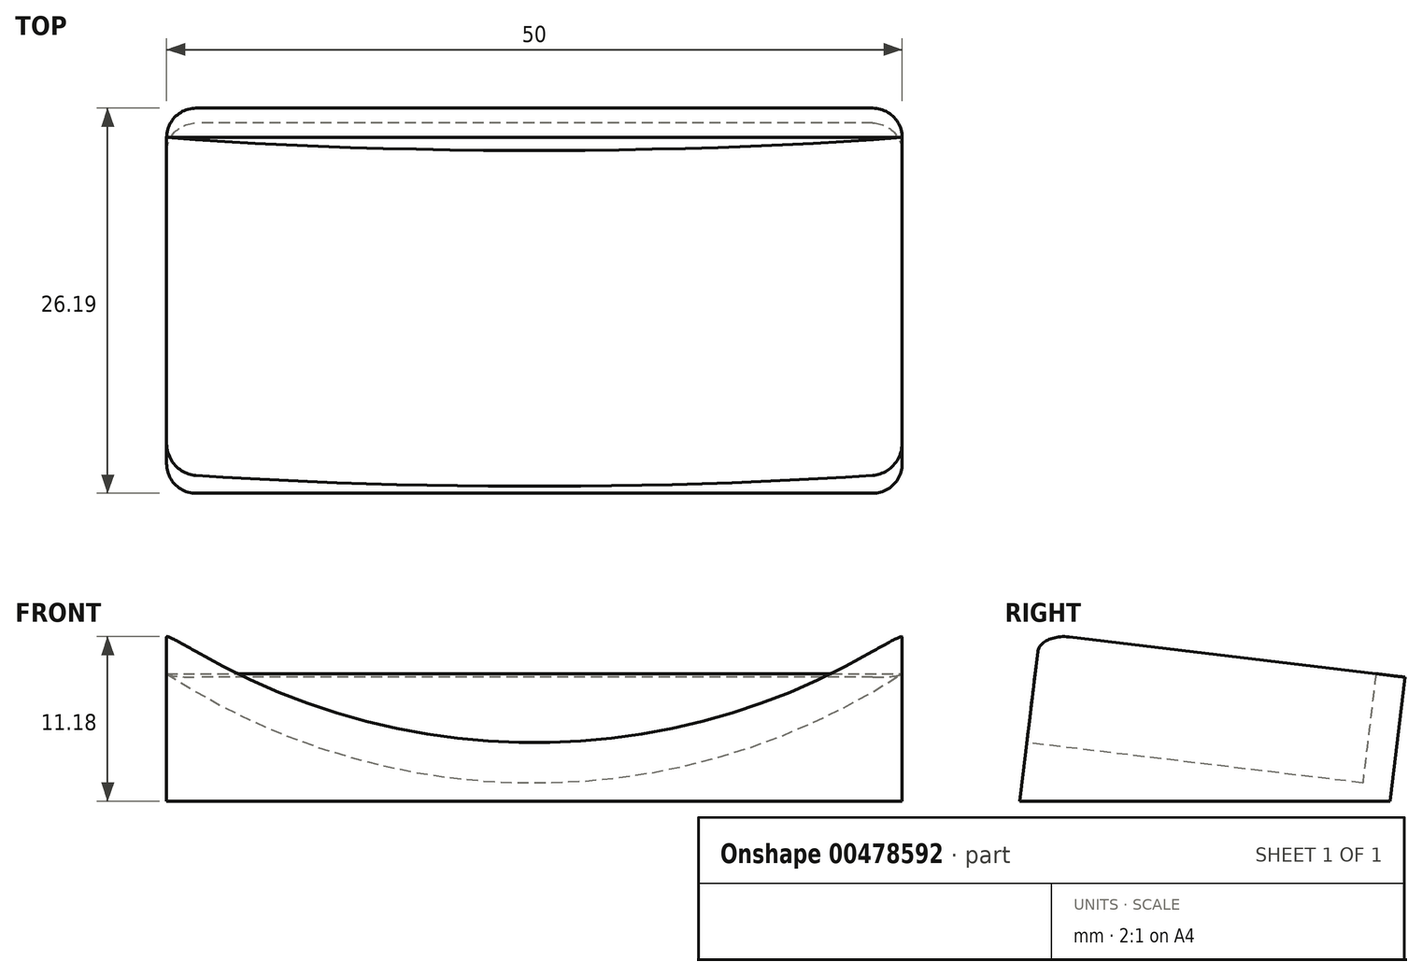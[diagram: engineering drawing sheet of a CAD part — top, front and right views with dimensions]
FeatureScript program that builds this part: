
annotation { "Feature Type Name" : "Feature", "Feature Type Description" : "" }
export const myFeature = defineFeature(function(context is Context, id is Id, definition is map)
    precondition{}
    {
        {
            var Q0;
            Q0=qCreatedBy(makeId("Right.planeOp"),FACE);
            var sketch = newSketch(context, id + "F0", { "sketchPlane" : qUnion([Q0])});
            skLineSegment(sketch, "E0", {"start": v(0, 0) * mm, "end": v(3, 25) * mm});
            skLineSegment(sketch, "E1", {"start": v(3, 25) * mm, "end": v(28.18, 25) * mm});
            skLineSegment(sketch, "E2", {"start": v(28.18, 25) * mm, "end": v(25.18, 0) * mm});
            skLineSegment(sketch, "E3", {"start": v(25.18, 0) * mm, "end": v(0, 0) * mm});
            skLineSegment(sketch, "E4", {"start": v(0, 25) * mm, "end": v(0, -29.38) * mm, "construction": true});
            skLineSegment(sketch, "E5", {"start": v(0, 25) * mm, "end": v(3, 25) * mm, "construction": true});
            skLineSegment(sketch, "E6", {"start": v(1.35, 11.22) * mm, "end": v(26.17, 8.24) * mm, "construction": true});
            skSolve(sketch);
        }
        {
            var Q0;
            Q0 = qSketchRegion(id + "F0", true);
            extrude(context, id + "F1", {"entities" : qUnion([Q0]), "depth" : 25 * mm, "hasSecondDirection" : true, "secondDirectionOppositeDirection" : true, "secondDirectionDepth" : 25 * mm});
        }
        {
            var Q0;
            Q0=makeQuery(id+"F1.opExtrude","SWEPT_FACE",FACE,{"disambiguationData":[OSD([sQuery(id+"F0.wireOp",EDGE,"E0")])]});
            var sketch = newSketch(context, id + "F2", { "sketchPlane" : qUnion([Q0])});
            skCircle(sketch, "E7", {"center": v(0, 49.5) * mm, "radius": 45.5 * mm});
            skSolve(sketch);
        }
        {
            var Q0;
            Q0 = qSketchRegion(id + "F2", true);
            extrude(context, id + "F3", {"entities" : qUnion([Q0]), "operationType" : NewBodyOperationType.REMOVE, "oppositeDirection" : true, "depth" : 23 * mm});
        }
        {
            var Q0;
            Q0=makeQuery(id+"F1.opExtrude","CAP_FACE",FACE,{"disambiguationData":[OSD([sQuery(id+"F0.wireOp",EDGE,"E0"),sQuery(id+"F0.wireOp",EDGE,"E1"),sQuery(id+"F0.wireOp",EDGE,"E2"),sQuery(id+"F0.wireOp",EDGE,"E3")])],"isStart":false});
            var sketch = newSketch(context, id + "F4", { "sketchPlane" : qUnion([Q0])});
            skLineSegment(sketch, "E8.0", {"start": v(1.37, 11.4) * mm, "end": v(24.2, 8.66) * mm, "construction": true});
            skLineSegment(sketch, "E9", {"start": v(24.23, 26.79) * mm, "end": v(22.09, 8.92) * mm});
            skLineSegment(sketch, "E10", {"start": v(22.09, 8.92) * mm, "end": v(36.98, 7.13) * mm});
            skLineSegment(sketch, "E11", {"start": v(36.98, 7.13) * mm, "end": v(39.13, 25) * mm});
            skLineSegment(sketch, "E12", {"start": v(39.13, 25) * mm, "end": v(24.23, 26.79) * mm});
            skSolve(sketch);
        }
        {
            var Q0;
            Q0 = qSketchRegion(id + "F4", true);
            extrude(context, id + "F5", {"entities" : qUnion([Q0]), "operationType" : NewBodyOperationType.REMOVE, "endBound" : BoundingType.THROUGH_ALL, "oppositeDirection" : true, "depth" : 25 * mm});
        }
        {
            var Q0;
            Q0=makeQuery(id+"F1.opExtrude","CAP_EDGE",EDGE,{"disambiguationData":[OSD([sQuery(id+"F0.wireOp",EDGE,"E0")])],"isStart":true});
            var Q1;
            Q1=makeQuery(id+"F1.opExtrude","CAP_EDGE",EDGE,{"disambiguationData":[OSD([sQuery(id+"F0.wireOp",EDGE,"E0")])],"isStart":false});
            var Q2;
            Q2=makeQuery(id+"F1.opExtrude","CAP_EDGE",EDGE,{"disambiguationData":[OSD([sQuery(id+"F0.wireOp",EDGE,"E2")])],"isStart":false});
            var Q3;
            Q3=makeQuery(id+"F1.opExtrude","CAP_EDGE",EDGE,{"disambiguationData":[OSD([sQuery(id+"F0.wireOp",EDGE,"E2")])],"isStart":true});
            fillet(context, id + "F6", {"entities" : qUnion([Q0, Q1, Q2, Q3]), "radius" : 2 * mm, "tangentPropagation" : true, "allowEdgeOverflow" : false});
        }
    });
